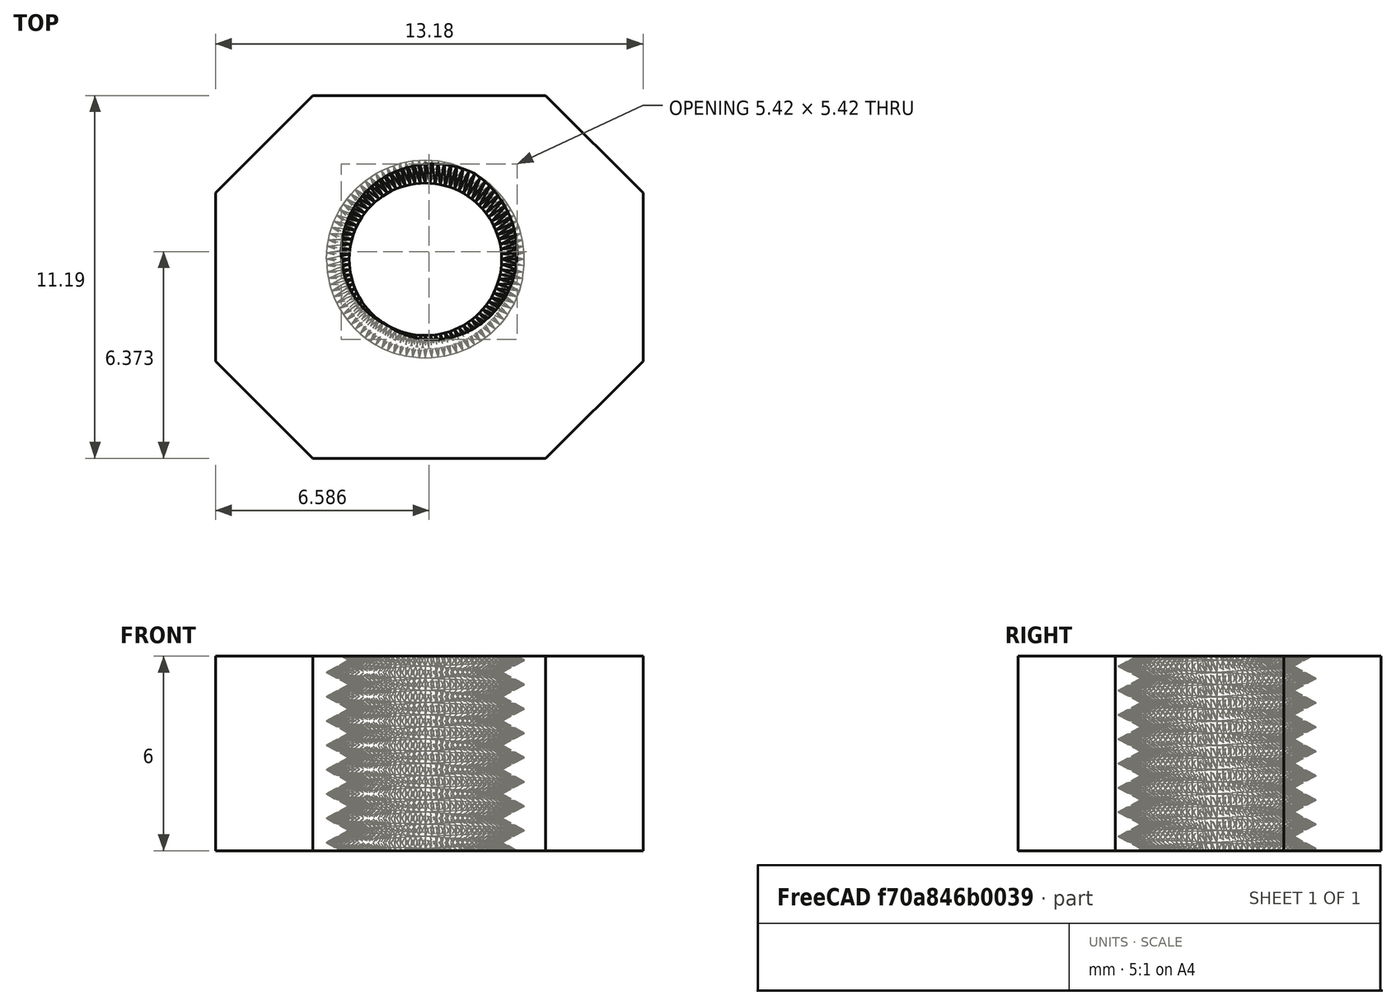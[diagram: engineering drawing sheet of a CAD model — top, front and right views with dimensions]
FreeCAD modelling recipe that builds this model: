
FCSTD DOCUMENT  (FreeCAD 1.0R39319 (Git))
Label: nut
License: All rights reserved
LicenseURL: https://en.wikipedia.org/wiki/All_rights_reserved
objects: Part::Feature×2, Mesh::Feature×1, Sketcher::SketchObject×1, PartDesign::Pad×1, PartDesign::Chamfer×1, PartDesign::Body×1, Part::Refine×1, Part::Cut×1
note: 13 computed .brp shape members not serialized (recipe doc carries the construction recipe); baked Part::Feature solids carry a one-line shape summary decoded from their .brp

FEATURE [Mesh::Feature] nut
FEATURE [Sketcher::SketchObject] Sketch
  ArcFitTolerance = 1e-06
  AttachmentSupport = -> [XY_Plane]
  FullyConstrained = false
  MakeInternals = false
  MapMode = 5
  sketch-geometry (4):
    g0: LineSegment StartX=-6.46547 StartY=5.05136 StartZ=0 EndX=-6.46547 EndY=-6.14378 EndZ=0
    g1: LineSegment StartX=-6.46547 StartY=-6.14378 StartZ=0 EndX=6.71111 EndY=-6.14378 EndZ=0
    g2: LineSegment StartX=6.71111 StartY=-6.14378 StartZ=0 EndX=6.71111 EndY=5.05136 EndZ=0
    g3: LineSegment StartX=6.71111 StartY=5.05136 StartZ=0 EndX=-6.46547 EndY=5.05136 EndZ=0
  constraints (8):
    c: Coincident(g0,g1)
    c: Coincident(g1,g2)
    c: Coincident(g2,g3)
    c: Coincident(g3,g0)
    c: Vertical(g0)
    c: Vertical(g2)
    c: Horizontal(g1)
    c: Horizontal(g3)
FEATURE [PartDesign::Pad] Pad
  Direction = (0,0,1)
  Length = 8
  Length2 = -2
  Profile = -> Sketch
  ReferenceAxis = -> Sketch [N_Axis]
  Refine = true
  Suppressed = false
  Type = 4
FEATURE [PartDesign::Chamfer] Chamfer
  Angle = 45
  Base = -> Pad [Edge2,Edge1,Edge5,Edge8]
  BaseFeature = -> Pad
  ChamferType = 0
  FlipDirection = false
  Refine = true
  Size = 3
  Size2 = 1
  SupportTransform = false
  Suppressed = false
  UseAllEdges = false
FEATURE [PartDesign::Body] Body
  AllowCompound = false
  Group = -> [Sketch,Pad,Chamfer]
  Origin = -> Origin
  Tip = -> Chamfer
FEATURE [Part::Feature] nut001
  shape: bbox 6.1 x 6.1 x 10 mm, 9024 faces, 0 solids (baked)
FEATURE [Part::Feature] nut001_solid  label="nut001 (Solid)"
  shape: bbox 6.1 x 6.1 x 10 mm, 9024 faces (baked)
FEATURE [Part::Refine] nut001_solid001  label="nut001 (Solid)001"
  Source = -> nut001_solid
FEATURE [Part::Cut] Cut
  Base = -> Body
  Tool = -> nut001_solid001
